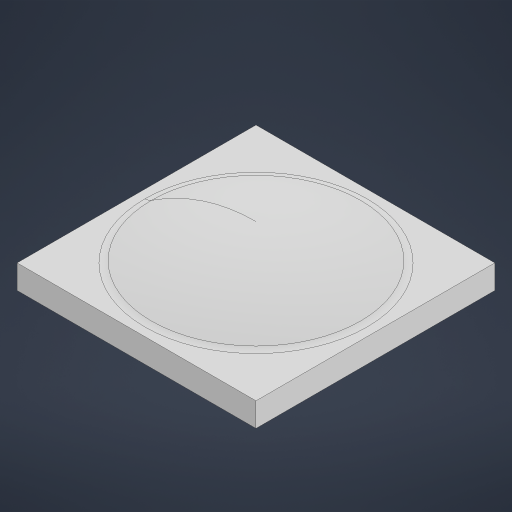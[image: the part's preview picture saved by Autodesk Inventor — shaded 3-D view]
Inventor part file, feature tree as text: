
AUTODESK INVENTOR PART (.ipt)
format: ipt  version: 2024.3 (Build 283343000, 343)  size: 231,424 bytes
history: native  units: mm
features: sketch x2, extrude x1, revolve x1, fillet x1
ambient origin geometry x8: Origin, YZ Plane, XZ Plane, XY Plane, X Axis, Y Axis, Z Axis, Center Point
bodies: Solid1 (feature_tree)
feature tree (5):
  sketch  "Sketch1"  dims[d0=100.0mm d1=30.0mm]
  sketch  "Sketch2"  dims[d2=5.0mm d3=10.0mm d4=0.0mm d6=90.0deg d7=5.0mm]
  extrude  "Extrusion1"  Depth=30.0mm
  revolve  "Revolution2"  [1 undecoded]
  fillet  "Fillet1"  [1 undecoded]
note: 2 required parameter values undecoded (feature->parameter linkage not recoverable at this tier; creation-order binding heuristic only, values carry confidence <= 0.55)